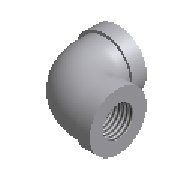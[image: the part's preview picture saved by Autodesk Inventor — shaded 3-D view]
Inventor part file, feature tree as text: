
AUTODESK INVENTOR PART (.ipt)
format: ipt  version: 2023.2 (Build 272271030, 271C)  size: 252,416 bytes
history: native  units: mm (DEFAULTED — no unit token found)
features: other x6, sketch x2, thread x2, sweep x1, revolve x1
ambient origin geometry x8: Origin, YZ Plane, XZ Plane, XY Plane, X Axis, Y Axis, Z Axis, Center Point
bodies: Solid1 (feature_tree)
feature tree (12):
  sketch  "Sketch1"  dims[d0=18.320766mm d1=27.94mm d2=30.48mm d3=6.35mm d4=10.922mm d5=0.312398mm d16=90.0deg]
  sweep  "Sweep1"
  revolve  "Revolution2"  Angle=90.0deg
  thread  "Thread1"  [1 undecoded]
  thread  "Thread2"  [1 undecoded]
  other  "Work Axis1"
  other  "Work Point1"
  other  "Work Point2"
  other  "Work Axis2"
  other  "Work Point3"
  other  "Work Point4"
  sketch  "Sketch3"  dims[d6=22.86mm d7=27.94mm d8=90.0deg d9=28.448mm d10=17.526mm d11=0.0mm d12=0.312398mm d13=10.922mm d14=6.35mm d15=18.320766mm d17=27.94mm d18=30.48mm d51=90.0deg d58=10.922mm d59=0.0mm d60=25.4mm d61=0.0mm d63=0.0mm]
note: 2 required parameter values undecoded (feature->parameter linkage not recoverable at this tier; creation-order binding heuristic only, values carry confidence <= 0.55)
